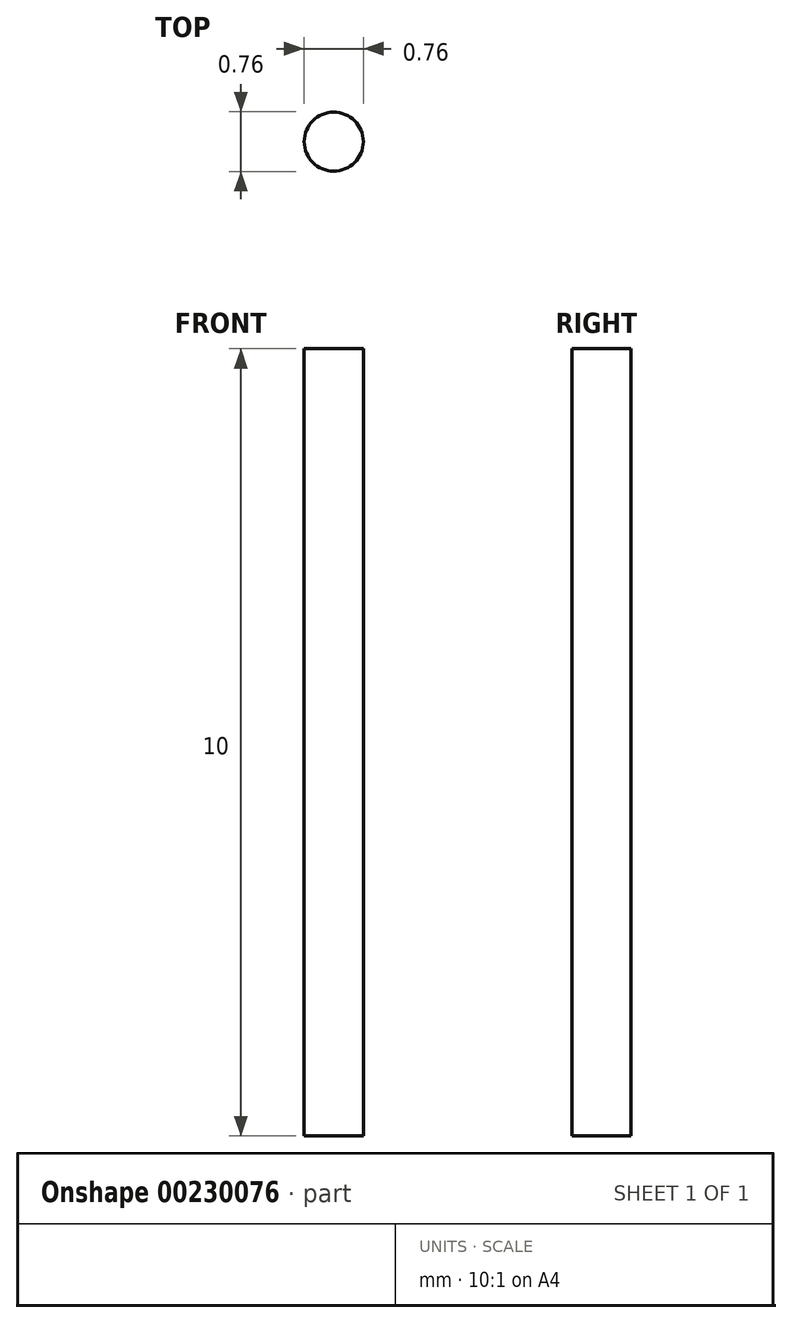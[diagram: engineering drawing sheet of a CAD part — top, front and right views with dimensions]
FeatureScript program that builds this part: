
annotation { "Feature Type Name" : "Feature", "Feature Type Description" : "" }
export const myFeature = defineFeature(function(context is Context, id is Id, definition is map)
    precondition{}
    {
        {
            var Q0;
            Q0=qCreatedBy(makeId("Top.planeOp"),FACE);
            var sketch = newSketch(context, id + "F0", { "sketchPlane" : qUnion([Q0])});
            skCircle(sketch, "E0", {"center": v(0, 0) * mm, "radius": 0.38 * mm});
            skSolve(sketch);
        }
        {
            var Q0;
            Q0=makeQuery(id+"F0.imprint","IMPRINT",FACE,{"disambiguationData":[TD([[makeQuery(id+"F0.imprint","IMPRINT",EDGE,{"derivedFrom":sQuery(id+"F0.wireOp",EDGE,"E0")}),1.0]])]});
            extrude(context, id + "F1", {"entities" : qUnion([Q0]), "depth" : 10 * mm});
        }
    });
